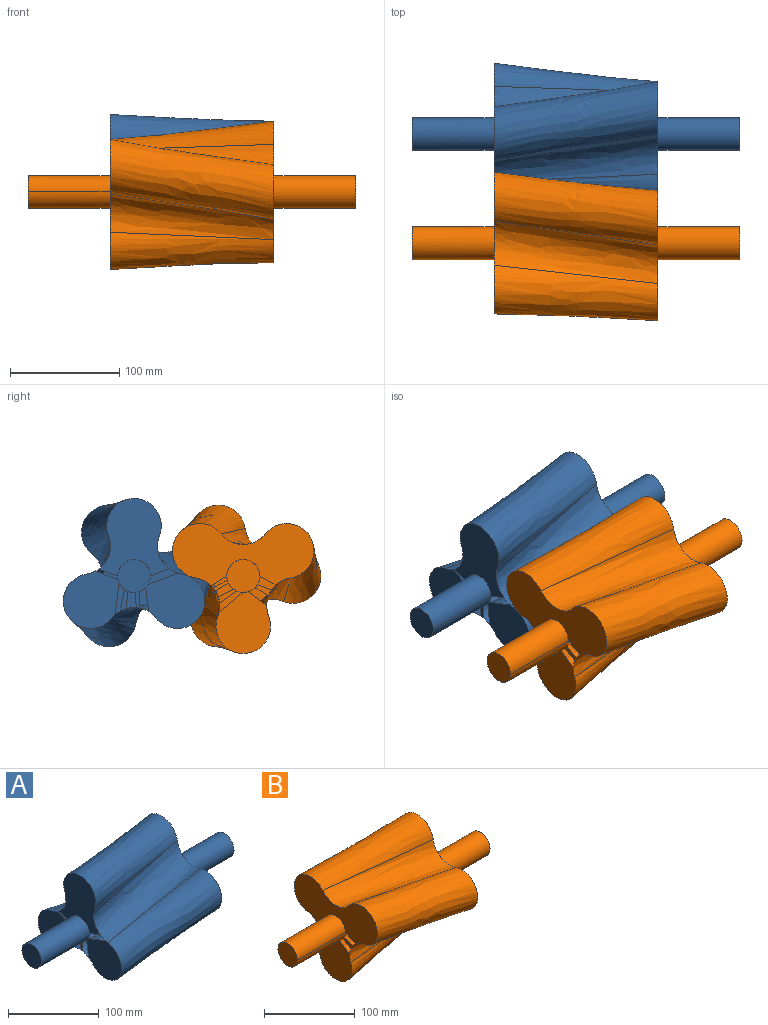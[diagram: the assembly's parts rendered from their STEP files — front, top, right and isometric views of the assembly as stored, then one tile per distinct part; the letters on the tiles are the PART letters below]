
ASSEMBLY  parts=2 mates=1
PART A: 12 faces, bbox 300x136.5x136.5 mm
  f0: plane 30.56x30mm, normal (1,0,0), area 706.8mm2, adj f1
  f1: cylinder r=15mm len=75mm, axis (-1,0,0), area 7068.6mm2, adj f0,f2
  f2: plane 130.31x119.64mm, normal (1,0,0), area 7673.9mm2, adj f1,f3,f4,f5,f6,f7,f8
  f3: bspline ~150x57.22mm, area 6861.3mm2, adj f2,f4,f8,f9
  f4: bspline ~150x66.66mm, area 14354.3mm2, adj f2,f3,f5,f9
  f5: bspline ~150x57.19mm, area 6861.2mm2, adj f2,f4,f6,f9
  f6: bspline ~150x72.96mm, area 14354.1mm2, adj f2,f5,f7,f9
  f7: bspline ~150x41.89mm, area 6861.3mm2, adj f2,f6,f8,f9
  f8: bspline ~150x73mm, area 14354.4mm2, adj f2,f3,f7,f9
  f9: plane 130.31x119.64mm, normal (-1,0,0), area 7320.5mm2, adj f3,f4,f5,f6,f7,f8,f11
  f10: plane 30.56x30mm, normal (-1,0,0), area 706.8mm2, adj f11
  f11: cylinder r=15mm len=75mm, axis (-1,0,0), area 7068.6mm2, adj f9,f10
PART B: 12 faces, bbox 300x136.5x136.5 mm
  f0: plane 30.56x30mm, normal (1,0,0), area 706.8mm2, adj f1
  f1: cylinder r=15mm len=75mm, axis (-1,0,0), area 7068.6mm2, adj f0,f2
  f2: plane 130.31x119.64mm, normal (1,0,0), area 7673.9mm2, adj f1,f3,f4,f5,f6,f7,f8
  f3: bspline ~150x41.89mm, area 6861.3mm2, adj f2,f4,f8,f9
  f4: bspline ~150x73.2mm, area 14354.3mm2, adj f2,f3,f5,f9
  f5: bspline ~150x57.2mm, area 6861.3mm2, adj f2,f4,f6,f9
  f6: bspline ~150x66.54mm, area 14354.2mm2, adj f2,f5,f7,f9
  f7: bspline ~150x57.19mm, area 6861.3mm2, adj f2,f6,f8,f9
  f8: bspline ~150x73.31mm, area 14354.3mm2, adj f2,f3,f7,f9
  f9: plane 130.31x119.64mm, normal (-1,0,0), area 7320.5mm2, adj f3,f4,f5,f6,f7,f8,f11
  f10: plane 30.56x30mm, normal (-1,0,0), area 706.8mm2, adj f11
  f11: cylinder r=15mm len=75mm, axis (-1,0,0), area 7068.6mm2, adj f9,f10
PLACE A t=(-74.64,2.52,-17.47)mm
PLACE B t=(-74.64,-97.48,-17.47)mm
MATE fastened A.f1 <-> B.f0  axis (1,0,0) through (0.36,2.52,-17.47)mm
